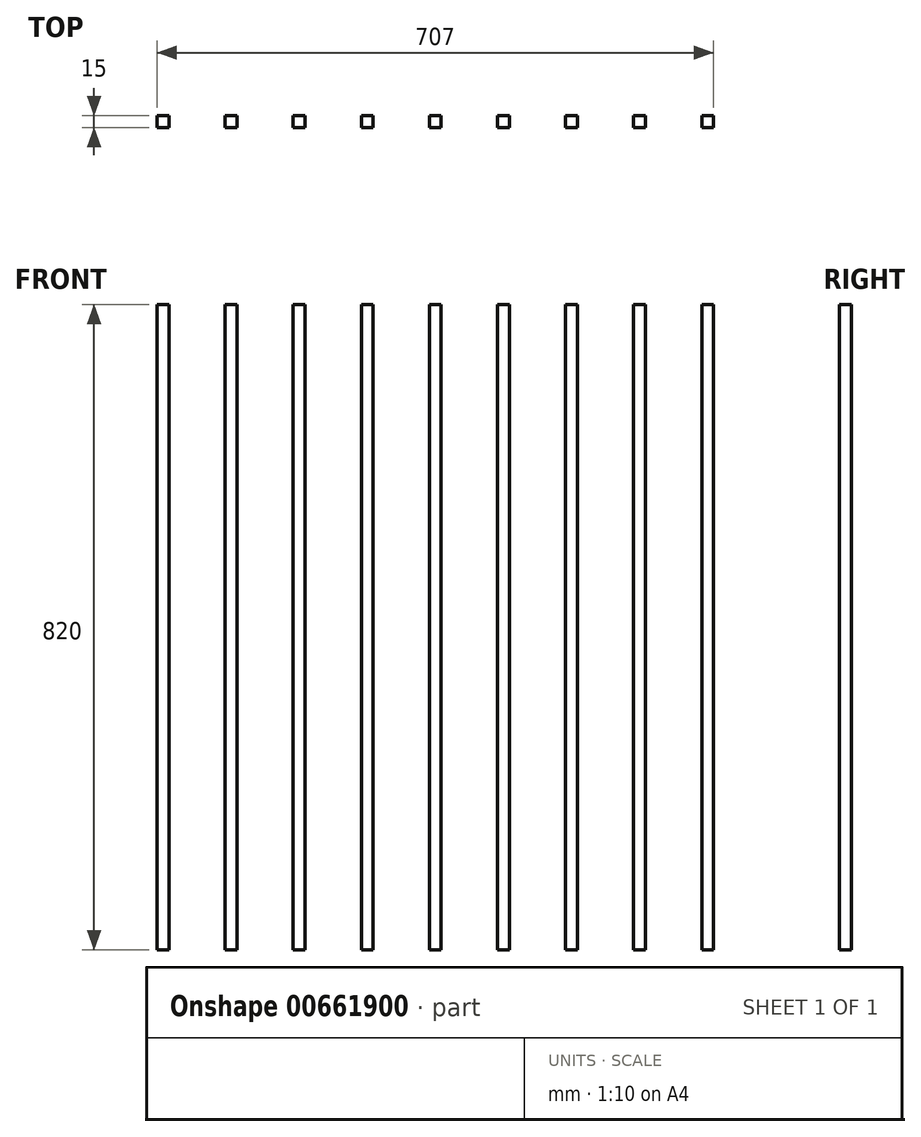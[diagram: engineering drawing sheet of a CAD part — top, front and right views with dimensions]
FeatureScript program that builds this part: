
annotation { "Feature Type Name" : "Feature", "Feature Type Description" : "" }
export const myFeature = defineFeature(function(context is Context, id is Id, definition is map)
    precondition{}
    {
        {
            var Q0;
            Q0=qCreatedBy(makeId("Front.planeOp"),FACE);
            var sketch = newSketch(context, id + "F0", { "sketchPlane" : qUnion([Q0])});
            skLineSegment(sketch, "E0.bottom", {"start": v(-68.37, 411.93) * mm, "end": v(-53.37, 411.93) * mm});
            skLineSegment(sketch, "E0.top", {"start": v(-68.37, -408.07) * mm, "end": v(-53.37, -408.07) * mm});
            skLineSegment(sketch, "E0.left", {"start": v(-68.37, 411.93) * mm, "end": v(-68.37, -408.07) * mm});
            skLineSegment(sketch, "E0.right", {"start": v(-53.37, 411.93) * mm, "end": v(-53.37, -408.07) * mm});
            skLineSegment(sketch, "E1", {"start": v(-17.62, 408.77) * mm, "end": v(-17.62, 342.7) * mm});
            skLineSegment(sketch, "E2.MirrorCS", {"start": v(18.13, 411.93) * mm, "end": v(18.13, -408.07) * mm});
            skLineSegment(sketch, "E3.MirrorCS", {"start": v(33.13, 411.93) * mm, "end": v(18.13, 411.93) * mm});
            skLineSegment(sketch, "E4.MirrorCS", {"start": v(33.13, 411.93) * mm, "end": v(33.13, -408.07) * mm});
            skLineSegment(sketch, "E5.MirrorCS", {"start": v(33.13, -408.07) * mm, "end": v(18.13, -408.07) * mm});
            skLineSegment(sketch, "E6", {"start": v(68.88, 406.34) * mm, "end": v(68.88, 341.45) * mm});
            skLineSegment(sketch, "E7.MirrorCS", {"start": v(104.63, 411.93) * mm, "end": v(104.63, -408.07) * mm});
            skLineSegment(sketch, "E8.MirrorCS", {"start": v(119.63, 411.93) * mm, "end": v(119.63, -408.07) * mm});
            skLineSegment(sketch, "E9.MirrorCS", {"start": v(104.63, 411.93) * mm, "end": v(119.63, 411.93) * mm});
            skLineSegment(sketch, "E10.MirrorCS", {"start": v(191.13, 411.93) * mm, "end": v(191.13, -408.07) * mm});
            skLineSegment(sketch, "E11.MirrorCS", {"start": v(206.13, 411.93) * mm, "end": v(206.13, -408.07) * mm});
            skLineSegment(sketch, "E12.MirrorCS", {"start": v(206.13, 411.93) * mm, "end": v(191.13, 411.93) * mm});
            skLineSegment(sketch, "E13.MirrorCS", {"start": v(104.63, -408.07) * mm, "end": v(119.63, -408.07) * mm});
            skLineSegment(sketch, "E14.MirrorCS", {"start": v(206.13, -408.07) * mm, "end": v(191.13, -408.07) * mm});
            skLineSegment(sketch, "E15", {"start": v(241.88, 414.35) * mm, "end": v(241.88, 313.64) * mm});
            skLineSegment(sketch, "E16.MirrorCS", {"start": v(277.63, 411.93) * mm, "end": v(277.63, -408.07) * mm});
            skLineSegment(sketch, "E17.MirrorCS", {"start": v(292.63, 411.93) * mm, "end": v(292.63, -408.07) * mm});
            skLineSegment(sketch, "E18.MirrorCS", {"start": v(364.13, 411.93) * mm, "end": v(364.13, -408.07) * mm});
            skLineSegment(sketch, "E19.MirrorCS", {"start": v(379.13, 411.93) * mm, "end": v(379.13, -408.07) * mm});
            skLineSegment(sketch, "E20.MirrorCS", {"start": v(450.63, 411.93) * mm, "end": v(450.63, -408.07) * mm});
            skLineSegment(sketch, "E21.MirrorCS", {"start": v(465.63, 411.93) * mm, "end": v(465.63, -408.07) * mm});
            skLineSegment(sketch, "E22.MirrorCS", {"start": v(537.13, 411.93) * mm, "end": v(537.13, -408.07) * mm});
            skLineSegment(sketch, "E23.MirrorCS", {"start": v(552.13, 411.93) * mm, "end": v(552.13, -408.07) * mm});
            skLineSegment(sketch, "E24.MirrorCS", {"start": v(552.13, 411.93) * mm, "end": v(537.13, 411.93) * mm});
            skLineSegment(sketch, "E25.MirrorCS", {"start": v(450.63, 411.93) * mm, "end": v(465.63, 411.93) * mm});
            skLineSegment(sketch, "E26.MirrorCS", {"start": v(379.13, 411.93) * mm, "end": v(364.13, 411.93) * mm});
            skLineSegment(sketch, "E27.MirrorCS", {"start": v(277.63, 411.93) * mm, "end": v(292.63, 411.93) * mm});
            skLineSegment(sketch, "E28.MirrorCS", {"start": v(552.13, -408.07) * mm, "end": v(537.13, -408.07) * mm});
            skLineSegment(sketch, "E29.MirrorCS", {"start": v(450.63, -408.07) * mm, "end": v(465.63, -408.07) * mm});
            skLineSegment(sketch, "E30.MirrorCS", {"start": v(379.13, -408.07) * mm, "end": v(364.13, -408.07) * mm});
            skLineSegment(sketch, "E31.MirrorCS", {"start": v(277.63, -408.07) * mm, "end": v(292.63, -408.07) * mm});
            skLineSegment(sketch, "E32", {"start": v(587.88, 434.76) * mm, "end": v(587.88, 319.3) * mm});
            skPoint(sketch, "E33.end.orphan", {"position": v(587.88, 318.97) * mm});
            skLineSegment(sketch, "E34.MirrorCS", {"start": v(623.63, 411.93) * mm, "end": v(623.63, -408.07) * mm});
            skLineSegment(sketch, "E35.MirrorCS", {"start": v(638.63, 411.93) * mm, "end": v(638.63, -408.07) * mm});
            skLineSegment(sketch, "E36.MirrorCS", {"start": v(623.63, 411.93) * mm, "end": v(638.63, 411.93) * mm});
            skLineSegment(sketch, "E37.MirrorCS", {"start": v(623.63, -408.07) * mm, "end": v(638.63, -408.07) * mm});
            skSolve(sketch);
        }
        {
            var Q0;
            Q0=makeQuery(id+"F0.imprint","IMPRINT",FACE,{"disambiguationData":[TD([[makeQuery(id+"F0.imprint","IMPRINT",EDGE,{"derivedFrom":sQuery(id+"F0.wireOp",EDGE,"E0.bottom")}),-1.0]])]});
            var Q1;
            Q1=makeQuery(id+"F0.imprint","IMPRINT",FACE,{"disambiguationData":[TD([[makeQuery(id+"F0.imprint","IMPRINT",EDGE,{"derivedFrom":sQuery(id+"F0.wireOp",EDGE,"E2.MirrorCS")}),1.0]])]});
            var Q2;
            Q2=makeQuery(id+"F0.imprint","IMPRINT",FACE,{"disambiguationData":[TD([[makeQuery(id+"F0.imprint","IMPRINT",EDGE,{"derivedFrom":sQuery(id+"F0.wireOp",EDGE,"E7.MirrorCS")}),1.0]])]});
            var Q3;
            Q3=makeQuery(id+"F0.imprint","IMPRINT",FACE,{"disambiguationData":[TD([[makeQuery(id+"F0.imprint","IMPRINT",EDGE,{"derivedFrom":sQuery(id+"F0.wireOp",EDGE,"E10.MirrorCS")}),1.0]])]});
            var Q4;
            Q4=makeQuery(id+"F0.imprint","IMPRINT",FACE,{"disambiguationData":[TD([[makeQuery(id+"F0.imprint","IMPRINT",EDGE,{"derivedFrom":sQuery(id+"F0.wireOp",EDGE,"E16.MirrorCS")}),1.0]])]});
            var Q5;
            Q5=makeQuery(id+"F0.imprint","IMPRINT",FACE,{"disambiguationData":[TD([[makeQuery(id+"F0.imprint","IMPRINT",EDGE,{"derivedFrom":sQuery(id+"F0.wireOp",EDGE,"E18.MirrorCS")}),1.0]])]});
            var Q6;
            Q6=makeQuery(id+"F0.imprint","IMPRINT",FACE,{"disambiguationData":[TD([[makeQuery(id+"F0.imprint","IMPRINT",EDGE,{"derivedFrom":sQuery(id+"F0.wireOp",EDGE,"E20.MirrorCS")}),1.0]])]});
            var Q7;
            Q7=makeQuery(id+"F0.imprint","IMPRINT",FACE,{"disambiguationData":[TD([[makeQuery(id+"F0.imprint","IMPRINT",EDGE,{"derivedFrom":sQuery(id+"F0.wireOp",EDGE,"E22.MirrorCS")}),1.0]])]});
            var Q8;
            Q8=makeQuery(id+"F0.imprint","IMPRINT",FACE,{"disambiguationData":[TD([[makeQuery(id+"F0.imprint","IMPRINT",EDGE,{"derivedFrom":sQuery(id+"F0.wireOp",EDGE,"E34.MirrorCS")}),1.0]])]});
            extrude(context, id + "F1", {"entities" : qUnion([Q0, Q1, Q2, Q3, Q4, Q5, Q6, Q7, Q8]), "depth" : 15 * mm, "offsetDistance" : 25 * mm});
        }
    });
